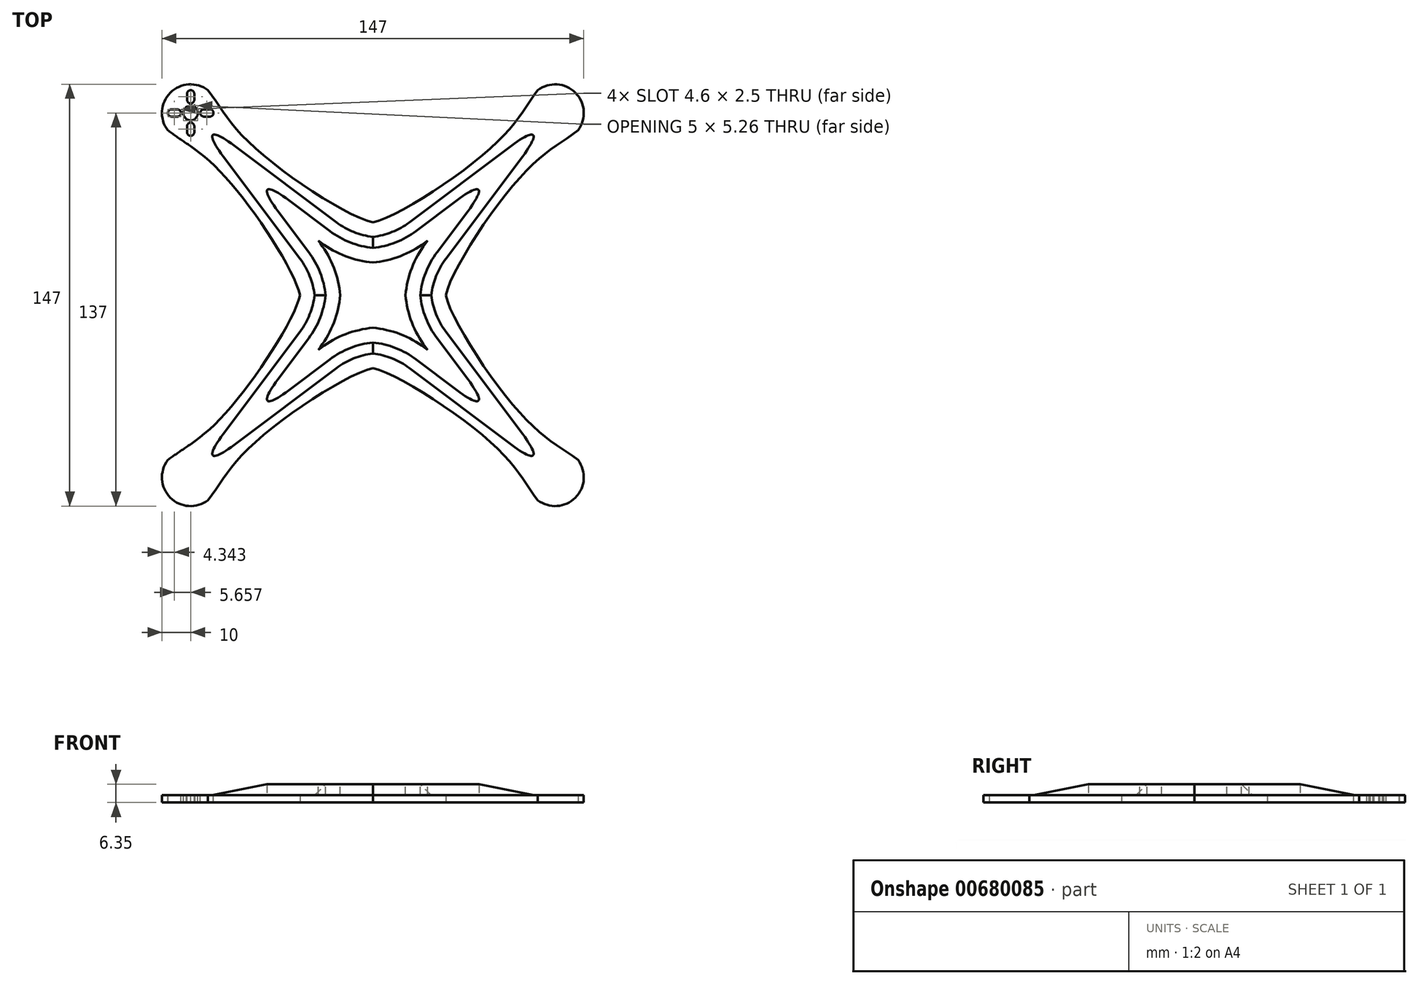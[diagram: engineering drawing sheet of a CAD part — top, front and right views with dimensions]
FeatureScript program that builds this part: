
annotation { "Feature Type Name" : "Feature", "Feature Type Description" : "" }
export const myFeature = defineFeature(function(context is Context, id is Id, definition is map)
    precondition{}
    {
        {
            var Q0;
            Q0=qCreatedBy(makeId("Top.planeOp"),FACE);
            var sketch = newSketch(context, id + "F0", { "sketchPlane" : qUnion([Q0])});
            skLineSegment(sketch, "E0", {"start": v(-50.8, 0) * mm, "end": v(50.8, 0) * mm, "construction": true});
            skLineSegment(sketch, "E1", {"start": v(0, 50.8) * mm, "end": v(0, -50.8) * mm, "construction": true});
            skLineSegment(sketch, "E2", {"start": v(0, 0) * mm, "end": v(-63.5, 63.5) * mm, "construction": true});
            skArc(sketch, "E3", {"start": v(-57.46, 71.47) * mm, "mid": v(-70.57, 70.57) * mm, "end": v(-71.47, 57.46) * mm});
            skLineSegment(sketch, "E4", {"start": v(0, 0) * mm, "end": v(0, 25.4) * mm});
            skFitSpline(sketch, "E5", {"points": [v(-57.46, 71.47) * mm, v(-42.48, 52.58) * mm, v(0, 25.4) * mm], "startDerivative": vector(33.33, -44.36) * mm, "endDerivative": vector(44.67, -9.8) * mm});
            skFitSpline(sketch, "E6.MirrorCS", {"points": [v(-71.47, 57.46) * mm, v(-52.58, 42.48) * mm, v(-25.4, 0) * mm], "startDerivative": vector(44.36, -33.33) * mm, "endDerivative": vector(9.8, -44.67) * mm});
            skFitSpline(sketch, "E7.MirrorCS", {"points": [v(-71.47, 57.46) * mm, v(-52.58, 42.48) * mm, v(-25.4, 0) * mm], "startDerivative": vector(44.36, -33.33) * mm, "endDerivative": vector(9.8, -44.67) * mm});
            skFitSpline(sketch, "E8.MirrorCS", {"points": [v(-57.46, 71.47) * mm, v(-42.48, 52.58) * mm, v(0, 25.4) * mm], "startDerivative": vector(33.33, -44.36) * mm, "endDerivative": vector(44.67, -9.8) * mm});
            skArc(sketch, "E9.MirrorCS", {"start": v(-71.47, 57.46) * mm, "mid": v(-70.57, 70.57) * mm, "end": v(-57.46, 71.47) * mm});
            skLineSegment(sketch, "E10.MirrorCS", {"start": v(0, 0) * mm, "end": v(-25.4, 0) * mm});
            skFitSpline(sketch, "E11.MirrorCS", {"points": [v(57.46, 71.47) * mm, v(42.48, 52.58) * mm, v(0, 25.4) * mm], "startDerivative": vector(-33.33, -44.36) * mm, "endDerivative": vector(-44.67, -9.8) * mm});
            skFitSpline(sketch, "E12.MirrorCS", {"points": [v(71.47, 57.46) * mm, v(52.58, 42.48) * mm, v(25.4, 0) * mm], "startDerivative": vector(-44.36, -33.33) * mm, "endDerivative": vector(-9.8, -44.67) * mm});
            skArc(sketch, "E13.MirrorCS", {"start": v(71.47, 57.46) * mm, "mid": v(70.57, 70.57) * mm, "end": v(57.46, 71.47) * mm});
            skFitSpline(sketch, "E14.MirrorCS", {"points": [v(-71.47, -57.46) * mm, v(-52.58, -42.48) * mm, v(-25.4, 0) * mm], "startDerivative": vector(44.36, 33.33) * mm, "endDerivative": vector(9.8, 44.67) * mm});
            skFitSpline(sketch, "E15.MirrorCS", {"points": [v(-57.46, -71.47) * mm, v(-42.48, -52.58) * mm, v(0, -25.4) * mm], "startDerivative": vector(33.33, 44.36) * mm, "endDerivative": vector(44.67, 9.8) * mm});
            skFitSpline(sketch, "E16.MirrorCS", {"points": [v(71.47, -57.46) * mm, v(52.58, -42.48) * mm, v(25.4, 0) * mm], "startDerivative": vector(-44.36, 33.33) * mm, "endDerivative": vector(-9.8, 44.67) * mm});
            skFitSpline(sketch, "E17.MirrorCS", {"points": [v(57.46, -71.47) * mm, v(42.48, -52.58) * mm, v(0, -25.4) * mm], "startDerivative": vector(-33.33, 44.36) * mm, "endDerivative": vector(-44.67, 9.8) * mm});
            skArc(sketch, "E18.MirrorCS", {"start": v(-71.47, -57.46) * mm, "mid": v(-70.57, -70.57) * mm, "end": v(-57.46, -71.47) * mm});
            skFitSpline(sketch, "E19.MirrorCS", {"points": [v(-71.47, -57.46) * mm, v(-52.58, -42.48) * mm, v(-25.4, 0) * mm], "startDerivative": vector(44.36, 33.33) * mm, "endDerivative": vector(9.8, 44.67) * mm});
            skArc(sketch, "E20.MirrorCS", {"start": v(-57.46, -71.47) * mm, "mid": v(-70.57, -70.57) * mm, "end": v(-71.47, -57.46) * mm});
            skArc(sketch, "E21.MirrorCS", {"start": v(71.47, -57.46) * mm, "mid": v(70.57, -70.57) * mm, "end": v(57.46, -71.47) * mm});
            skLineSegment(sketch, "E22.MirrorCS", {"start": v(0, 0) * mm, "end": v(0, -25.4) * mm});
            skLineSegment(sketch, "E23.MirrorCS", {"start": v(0, 0) * mm, "end": v(-63.5, -63.5) * mm, "construction": true});
            skLineSegment(sketch, "E24", {"start": v(-63.5, -63.5) * mm, "end": v(-63.5, 63.5) * mm});
            skSolve(sketch);
        }
        {
            var Q0;
            Q0=makeQuery(id+"F0.imprint","IMPRINT",FACE,{"disambiguationData":[TD([[makeQuery(id+"F0.imprint","IMPRINT",EDGE,{"derivedFrom":sQuery(id+"F0.wireOp",EDGE,"E4")}),-1.0]])]});
            var Q1;
            Q1=makeQuery(id+"F0.imprint","IMPRINT",FACE,{"disambiguationData":[TD([[makeQuery(id+"F0.imprint","IMPRINT",EDGE,{"derivedFrom":sQuery(id+"F0.wireOp",EDGE,"E10.MirrorCS")}),1.0]])]});
            var Q2;
            Q2=makeQuery(id+"F0.imprint","IMPRINT",FACE,{"disambiguationData":[TD([[makeQuery(id+"F0.imprint","IMPRINT",EDGE,{"derivedFrom":sQuery(id+"F0.wireOp",EDGE,"E4")}),1.0]])]});
            extrude(context, id + "F1", {"entities" : qUnion([Q0, Q1, Q2]), "depth" : 2.54 * mm, "offsetDistance" : 25.4 * mm, "symmetric" : true});
        }
        {
            var Q0;
            Q0=makeQuery(id+"F1.opExtrude","CAP_FACE",FACE,{"disambiguationData":[OSD([sQuery(id+"F0.wireOp",EDGE,"E7.MirrorCS"),sQuery(id+"F0.wireOp",EDGE,"E8.MirrorCS"),sQuery(id+"F0.wireOp",EDGE,"E9.MirrorCS"),sQuery(id+"F0.wireOp",EDGE,"E11.MirrorCS"),sQuery(id+"F0.wireOp",EDGE,"E12.MirrorCS"),sQuery(id+"F0.wireOp",EDGE,"E13.MirrorCS"),sQuery(id+"F0.wireOp",EDGE,"E16.MirrorCS"),sQuery(id+"F0.wireOp",EDGE,"E17.MirrorCS"),sQuery(id+"F0.wireOp",EDGE,"E15.MirrorCS"),sQuery(id+"F0.wireOp",EDGE,"E19.MirrorCS"),sQuery(id+"F0.wireOp",EDGE,"E20.MirrorCS"),sQuery(id+"F0.wireOp",EDGE,"E21.MirrorCS")])],"isStart":false});
            var sketch = newSketch(context, id + "F2", { "sketchPlane" : qUnion([Q0])});
            skCircle(sketch, "E25", {"center": v(-57.84, 63.5) * mm, "radius": 1.25 * mm, "construction": true});
            skCircle(sketch, "E26", {"center": v(-63.5, 57.84) * mm, "radius": 1.25 * mm, "construction": true});
            skCircle(sketch, "E27", {"center": v(-63.5, 69.16) * mm, "radius": 1.25 * mm, "construction": true});
            skCircle(sketch, "E28", {"center": v(-69.16, 63.5) * mm, "radius": 1.25 * mm, "construction": true});
            skLineSegment(sketch, "E29", {"start": v(-63.5, 69.16) * mm, "end": v(-69.16, 63.5) * mm, "construction": true});
            skLineSegment(sketch, "E30", {"start": v(-63.5, 57.84) * mm, "end": v(-69.16, 63.5) * mm, "construction": true});
            skLineSegment(sketch, "E31", {"start": v(-57.84, 63.5) * mm, "end": v(-63.5, 57.84) * mm, "construction": true});
            skLineSegment(sketch, "E32", {"start": v(-57.84, 63.5) * mm, "end": v(-63.5, 69.16) * mm, "construction": true});
            skLineSegment(sketch, "E33", {"start": v(-69.16, 63.5) * mm, "end": v(-57.84, 63.5) * mm, "construction": true});
            skArc(sketch, "E34", {"start": v(-64.75, 68.1) * mm, "mid": v(-63.5, 66.86) * mm, "end": v(-62.25, 68.1) * mm});
            skArc(sketch, "E35", {"start": v(-62.25, 70.2) * mm, "mid": v(-63.5, 71.46) * mm, "end": v(-64.75, 70.2) * mm});
            skLineSegment(sketch, "E36", {"start": v(-64.75, 68.1) * mm, "end": v(-64.75, 70.2) * mm});
            skLineSegment(sketch, "E37", {"start": v(-62.25, 70.2) * mm, "end": v(-62.25, 68.1) * mm});
            skLineSegment(sketch, "E38", {"start": v(-63.5, 68.1) * mm, "end": v(-63.5, 70.2) * mm, "construction": true});
            skArc(sketch, "E39", {"start": v(-58.9, 64.75) * mm, "mid": v(-60.14, 63.5) * mm, "end": v(-58.9, 62.25) * mm});
            skArc(sketch, "E40", {"start": v(-56.8, 62.25) * mm, "mid": v(-55.54, 63.5) * mm, "end": v(-56.8, 64.75) * mm});
            skLineSegment(sketch, "E41", {"start": v(-58.9, 64.75) * mm, "end": v(-56.8, 64.75) * mm});
            skLineSegment(sketch, "E42", {"start": v(-56.8, 62.25) * mm, "end": v(-58.9, 62.25) * mm});
            skLineSegment(sketch, "E43", {"start": v(-58.9, 63.5) * mm, "end": v(-56.8, 63.5) * mm, "construction": true});
            skArc(sketch, "E44", {"start": v(-64.75, 56.8) * mm, "mid": v(-63.5, 55.54) * mm, "end": v(-62.25, 56.8) * mm});
            skArc(sketch, "E45", {"start": v(-62.25, 58.9) * mm, "mid": v(-63.5, 60.14) * mm, "end": v(-64.75, 58.9) * mm});
            skLineSegment(sketch, "E46", {"start": v(-64.75, 56.8) * mm, "end": v(-64.75, 58.9) * mm});
            skLineSegment(sketch, "E47", {"start": v(-62.25, 58.9) * mm, "end": v(-62.25, 56.8) * mm});
            skLineSegment(sketch, "E48", {"start": v(-63.5, 56.8) * mm, "end": v(-63.5, 58.9) * mm, "construction": true});
            skArc(sketch, "E49", {"start": v(-70.2, 64.75) * mm, "mid": v(-71.46, 63.5) * mm, "end": v(-70.2, 62.25) * mm});
            skArc(sketch, "E50", {"start": v(-68.1, 62.25) * mm, "mid": v(-66.86, 63.5) * mm, "end": v(-68.1, 64.75) * mm});
            skLineSegment(sketch, "E51", {"start": v(-70.2, 64.75) * mm, "end": v(-68.1, 64.75) * mm});
            skLineSegment(sketch, "E52", {"start": v(-68.1, 62.25) * mm, "end": v(-70.2, 62.25) * mm});
            skLineSegment(sketch, "E53", {"start": v(-70.2, 63.5) * mm, "end": v(-68.1, 63.5) * mm, "construction": true});
            skLineSegment(sketch, "E54", {"start": v(-63.5, 69.16) * mm, "end": v(-63.5, 57.84) * mm, "construction": true});
            skCircle(sketch, "E55.cCircle", {"center": v(-63.5, 63.5) * mm, "radius": 2.5 * mm, "construction": true});
            skLineSegment(sketch, "E55.0", {"start": v(-61, 62.69) * mm, "end": v(-61.95, 61.37) * mm});
            skLineSegment(sketch, "E55.1", {"start": v(-61.95, 61.37) * mm, "end": v(-63.5, 60.87) * mm});
            skLineSegment(sketch, "E55.2", {"start": v(-63.5, 60.87) * mm, "end": v(-65.05, 61.37) * mm});
            skLineSegment(sketch, "E55.3", {"start": v(-65.05, 61.37) * mm, "end": v(-66, 62.69) * mm});
            skLineSegment(sketch, "E55.4", {"start": v(-66, 62.69) * mm, "end": v(-66, 64.31) * mm});
            skLineSegment(sketch, "E55.5", {"start": v(-66, 64.31) * mm, "end": v(-65.05, 65.63) * mm});
            skLineSegment(sketch, "E55.6", {"start": v(-65.05, 65.63) * mm, "end": v(-63.5, 66.13) * mm});
            skLineSegment(sketch, "E55.7", {"start": v(-63.5, 66.13) * mm, "end": v(-61.95, 65.63) * mm});
            skLineSegment(sketch, "E55.8", {"start": v(-61.95, 65.63) * mm, "end": v(-61, 64.31) * mm});
            skLineSegment(sketch, "E55.9", {"start": v(-61, 64.31) * mm, "end": v(-61, 62.69) * mm});
            skPoint(sketch, "E55.0.midPoint", {"position": v(-61.48, 62.03) * mm});
            skSolve(sketch);
        }
        {
            var Q0;
            Q0 = qSketchRegion(id + "F2", true);
            extrude(context, id + "F3", {"entities" : qUnion([Q0]), "operationType" : NewBodyOperationType.REMOVE, "endBound" : BoundingType.THROUGH_ALL, "oppositeDirection" : true, "depth" : 25.4 * mm, "offsetDistance" : 25.4 * mm});
        }
        {
            var Q0;
            Q0=makeQuery(id+"F1.opExtrude","CAP_FACE",FACE,{"disambiguationData":[OSD([sQuery(id+"F0.wireOp",EDGE,"E7.MirrorCS"),sQuery(id+"F0.wireOp",EDGE,"E8.MirrorCS"),sQuery(id+"F0.wireOp",EDGE,"E9.MirrorCS"),sQuery(id+"F0.wireOp",EDGE,"E11.MirrorCS"),sQuery(id+"F0.wireOp",EDGE,"E12.MirrorCS"),sQuery(id+"F0.wireOp",EDGE,"E13.MirrorCS"),sQuery(id+"F0.wireOp",EDGE,"E16.MirrorCS"),sQuery(id+"F0.wireOp",EDGE,"E17.MirrorCS"),sQuery(id+"F0.wireOp",EDGE,"E15.MirrorCS"),sQuery(id+"F0.wireOp",EDGE,"E19.MirrorCS"),sQuery(id+"F0.wireOp",EDGE,"E20.MirrorCS"),sQuery(id+"F0.wireOp",EDGE,"E21.MirrorCS")])],"isStart":false});
            var sketch = newSketch(context, id + "F4", { "sketchPlane" : qUnion([Q0])});
            skLineSegment(sketch, "E56", {"start": v(-63.5, -63.5) * mm, "end": v(0, 0) * mm, "construction": true});
            skLineSegment(sketch, "E57", {"start": v(0, 0) * mm, "end": v(0, -25.4) * mm, "construction": true});
            skLineSegment(sketch, "E58", {"start": v(0, -25.4) * mm, "end": v(-25.4, -25.4) * mm, "construction": true});
            skLineSegment(sketch, "E59", {"start": v(-25.4, -25.4) * mm, "end": v(-25.4, 0) * mm, "construction": true});
            skLineSegment(sketch, "E60", {"start": v(-25.4, 0) * mm, "end": v(0, 0) * mm, "construction": true});
            skLineSegment(sketch, "E61", {"start": v(-63.5, -63.5) * mm, "end": v(-25.4, -12.7) * mm});
            skLineSegment(sketch, "E62", {"start": v(-63.5, -63.5) * mm, "end": v(-12.7, -25.4) * mm});
            skArc(sketch, "E63", {"start": v(0, -20.32) * mm, "mid": v(-6.69, -22.02) * mm, "end": v(-12.7, -25.4) * mm});
            skArc(sketch, "E64.MirrorCS", {"start": v(-20.32, 0) * mm, "mid": v(-22.02, -6.69) * mm, "end": v(-25.4, -12.7) * mm});
            skArc(sketch, "E65.1.0", {"start": v(0, -20.32) * mm, "mid": v(6.69, -22.02) * mm, "end": v(12.7, -25.4) * mm});
            skLineSegment(sketch, "E65.1.1", {"start": v(63.5, -63.5) * mm, "end": v(12.7, -25.4) * mm});
            skLineSegment(sketch, "E65.1.2", {"start": v(63.5, -63.5) * mm, "end": v(25.4, -12.7) * mm});
            skArc(sketch, "E65.1.3", {"start": v(20.32, 0) * mm, "mid": v(22.02, -6.69) * mm, "end": v(25.4, -12.7) * mm});
            skArc(sketch, "E65.2.0", {"start": v(20.32, 0) * mm, "mid": v(22.02, 6.69) * mm, "end": v(25.4, 12.7) * mm});
            skLineSegment(sketch, "E65.2.1", {"start": v(63.5, 63.5) * mm, "end": v(25.4, 12.7) * mm});
            skLineSegment(sketch, "E65.2.2", {"start": v(63.5, 63.5) * mm, "end": v(12.7, 25.4) * mm});
            skArc(sketch, "E65.2.3", {"start": v(0, 20.32) * mm, "mid": v(6.69, 22.02) * mm, "end": v(12.7, 25.4) * mm});
            skArc(sketch, "E65.3.0", {"start": v(0, 20.32) * mm, "mid": v(-6.69, 22.02) * mm, "end": v(-12.7, 25.4) * mm});
            skLineSegment(sketch, "E65.3.1", {"start": v(-63.5, 63.5) * mm, "end": v(-12.7, 25.4) * mm});
            skLineSegment(sketch, "E65.3.2", {"start": v(-63.5, 63.5) * mm, "end": v(-25.4, 12.7) * mm});
            skArc(sketch, "E65.3.3", {"start": v(-20.32, 0) * mm, "mid": v(-22.02, 6.69) * mm, "end": v(-25.4, 12.7) * mm});
            skPoint(sketch, "E65.center", {"position": v(0, 0) * mm});
            skSolve(sketch);
        }
        {
            var Q0;
            Q0=makeQuery(id+"F4.imprint","IMPRINT",FACE,{"disambiguationData":[TD([[makeQuery(id+"F4.imprint","IMPRINT",EDGE,{"derivedFrom":sQuery(id+"F4.wireOp",EDGE,"E61")}),-1.0]])]});
            var Q1;
            {var subQ18=sQuery(id+"F4.wireOp",EDGE,"E63");Q1=makeQuery(id+"F4.imprint","IMPRINT",FACE,{"disambiguationData":[TD([[makeQuery(id+"F4.imprint","IMPRINT",EDGE,{"derivedFrom":subQ18}),-1.0]])]});}
            extrude(context, id + "F5", {"entities" : qUnion([Q0, Q1]), "operationType" : NewBodyOperationType.ADD, "depth" : 3.8 * mm, "offsetDistance" : 25.4 * mm});
        }
        {
            var Q0;
            Q0=makeQuery(id+"F5.opExtrude","CAP_FACE",FACE,{"disambiguationData":[OSD([sQuery(id+"F2.wireOp",EDGE,"E55.0"),sQuery(id+"F4.wireOp",EDGE,"E61"),sQuery(id+"F4.wireOp",EDGE,"E62"),sQuery(id+"F4.wireOp",EDGE,"E63"),sQuery(id+"F4.wireOp",EDGE,"E64.MirrorCS"),sQuery(id+"F4.wireOp",EDGE,"E65.1.0"),sQuery(id+"F4.wireOp",EDGE,"E65.1.1"),sQuery(id+"F4.wireOp",EDGE,"E65.1.2"),sQuery(id+"F4.wireOp",EDGE,"E65.1.3"),sQuery(id+"F4.wireOp",EDGE,"E65.2.0"),sQuery(id+"F4.wireOp",EDGE,"E65.2.1"),sQuery(id+"F4.wireOp",EDGE,"E65.2.2"),sQuery(id+"F4.wireOp",EDGE,"E65.2.3"),sQuery(id+"F4.wireOp",EDGE,"E65.3.0"),sQuery(id+"F4.wireOp",EDGE,"E65.3.1"),sQuery(id+"F4.wireOp",EDGE,"E65.3.2"),sQuery(id+"F4.wireOp",EDGE,"E65.3.3")])],"isStart":false});
            chamfer(context, id + "F6", {"entities" : qUnion([Q0]), "width" : 3.8 * mm, "tangentPropagation" : true});
        }
        {
            var Q0;
            Q0=makeQuery(id+"F6.opChamfer","BLEND_EDGE",EDGE,{"blendedFrom":[makeQuery(id+"F5.opExtrude","CAP_EDGE",EDGE,{"disambiguationData":[OSD([sQuery(id+"F4.wireOp",EDGE,"E61")])],"isStart":false}),makeQuery(id+"F5.opExtrude","CAP_EDGE",EDGE,{"disambiguationData":[OSD([sQuery(id+"F4.wireOp",EDGE,"E62")])],"isStart":false})],"blendedInto":[]});
            var Q1;
            Q1=makeQuery(id+"F6.opChamfer","BLEND_EDGE",EDGE,{"blendedFrom":[makeQuery(id+"F5.opExtrude","CAP_EDGE",EDGE,{"disambiguationData":[OSD([sQuery(id+"F4.wireOp",EDGE,"E65.3.1")])],"isStart":false}),makeQuery(id+"F5.opExtrude","CAP_EDGE",EDGE,{"disambiguationData":[OSD([sQuery(id+"F4.wireOp",EDGE,"E65.3.2")])],"isStart":false})],"blendedInto":[]});
            var Q2;
            Q2=makeQuery(id+"F6.opChamfer","BLEND_EDGE",EDGE,{"blendedFrom":[makeQuery(id+"F5.opExtrude","CAP_EDGE",EDGE,{"disambiguationData":[OSD([sQuery(id+"F4.wireOp",EDGE,"E65.1.1")])],"isStart":false}),makeQuery(id+"F5.opExtrude","CAP_EDGE",EDGE,{"disambiguationData":[OSD([sQuery(id+"F4.wireOp",EDGE,"E65.1.2")])],"isStart":false})],"blendedInto":[]});
            var Q3;
            Q3=makeQuery(id+"F6.opChamfer","BLEND_EDGE",EDGE,{"blendedFrom":[makeQuery(id+"F5.opExtrude","CAP_EDGE",EDGE,{"disambiguationData":[OSD([sQuery(id+"F4.wireOp",EDGE,"E65.2.1")])],"isStart":false}),makeQuery(id+"F5.opExtrude","CAP_EDGE",EDGE,{"disambiguationData":[OSD([sQuery(id+"F4.wireOp",EDGE,"E65.2.2")])],"isStart":false})],"blendedInto":[]});
            fillet(context, id + "F7", {"entities" : qUnion([Q0, Q1, Q2, Q3]), "radius" : 3.8 * mm, "tangentPropagation" : true, "defaultsChanged" : false, "vertexSettings" : [], "allowEdgeOverflow" : false});
        }
        {
            var Q0;
            Q0=makeQuery(id+"F5.opExtrude","CAP_FACE",FACE,{"disambiguationData":[OSD([sQuery(id+"F2.wireOp",EDGE,"E55.0"),sQuery(id+"F4.wireOp",EDGE,"E61"),sQuery(id+"F4.wireOp",EDGE,"E62"),sQuery(id+"F4.wireOp",EDGE,"E63"),sQuery(id+"F4.wireOp",EDGE,"E64.MirrorCS"),sQuery(id+"F4.wireOp",EDGE,"E65.1.0"),sQuery(id+"F4.wireOp",EDGE,"E65.1.1"),sQuery(id+"F4.wireOp",EDGE,"E65.1.2"),sQuery(id+"F4.wireOp",EDGE,"E65.1.3"),sQuery(id+"F4.wireOp",EDGE,"E65.2.0"),sQuery(id+"F4.wireOp",EDGE,"E65.2.1"),sQuery(id+"F4.wireOp",EDGE,"E65.2.2"),sQuery(id+"F4.wireOp",EDGE,"E65.2.3"),sQuery(id+"F4.wireOp",EDGE,"E65.3.0"),sQuery(id+"F4.wireOp",EDGE,"E65.3.1"),sQuery(id+"F4.wireOp",EDGE,"E65.3.2"),sQuery(id+"F4.wireOp",EDGE,"E65.3.3")])],"isStart":false});
            var sketch = newSketch(context, id + "F8", { "sketchPlane" : qUnion([Q0])});
            skLineSegment(sketch, "E66.0.0", {"start": v(14.99, -22.35) * mm, "end": v(29.36, -33.13) * mm});
            skEllipticalArc(sketch, "E66.0.1", {});
            skLineSegment(sketch, "E66.0.2", {"start": v(33.13, -29.36) * mm, "end": v(22.35, -14.99) * mm});
            skArc(sketch, "E66.0.3", {"start": v(22.35, -14.99) * mm, "mid": v(18.4, -7.9) * mm, "end": v(16.49, 0) * mm});
            skArc(sketch, "E66.0.4", {"start": v(16.49, 0) * mm, "mid": v(18.4, 7.9) * mm, "end": v(22.35, 14.99) * mm});
            skLineSegment(sketch, "E66.0.5", {"start": v(22.35, 14.99) * mm, "end": v(33.13, 29.36) * mm});
            skEllipticalArc(sketch, "E66.0.6", {});
            skLineSegment(sketch, "E66.0.7", {"start": v(29.36, 33.13) * mm, "end": v(14.99, 22.35) * mm});
            skArc(sketch, "E66.0.8", {"start": v(14.99, 22.35) * mm, "mid": v(7.9, 18.4) * mm, "end": v(0, 16.49) * mm});
            skArc(sketch, "E66.0.9", {"start": v(0, 16.49) * mm, "mid": v(-7.9, 18.4) * mm, "end": v(-14.99, 22.35) * mm});
            skLineSegment(sketch, "E66.0.10", {"start": v(-14.99, 22.35) * mm, "end": v(-29.36, 33.13) * mm});
            skEllipticalArc(sketch, "E66.0.11", {});
            skLineSegment(sketch, "E66.0.12", {"start": v(-33.13, 29.36) * mm, "end": v(-22.35, 14.99) * mm});
            skArc(sketch, "E66.0.13", {"start": v(-22.35, 14.99) * mm, "mid": v(-18.4, 7.9) * mm, "end": v(-16.49, 0) * mm});
            skArc(sketch, "E66.0.14", {"start": v(-16.49, 0) * mm, "mid": v(-18.4, -7.9) * mm, "end": v(-22.35, -14.99) * mm});
            skLineSegment(sketch, "E66.0.15", {"start": v(-22.35, -14.99) * mm, "end": v(-33.13, -29.36) * mm});
            skEllipticalArc(sketch, "E66.0.16", {});
            skLineSegment(sketch, "E66.0.17", {"start": v(-29.36, -33.13) * mm, "end": v(-14.99, -22.35) * mm});
            skArc(sketch, "E66.0.18", {"start": v(-14.99, -22.35) * mm, "mid": v(-7.9, -18.4) * mm, "end": v(0, -16.49) * mm});
            skArc(sketch, "E66.0.19", {"start": v(0, -16.49) * mm, "mid": v(7.9, -18.4) * mm, "end": v(14.99, -22.35) * mm});
            skArc(sketch, "E67.0", {"start": v(0, -11.38) * mm, "mid": v(9.5, -13.58) * mm, "end": v(18.03, -18.29) * mm});
            skArc(sketch, "E67.1", {"start": v(-18.03, -18.29) * mm, "mid": v(-9.5, -13.58) * mm, "end": v(0, -11.38) * mm});
            skLineSegment(sketch, "E67.2", {"start": v(-19.05, -19.05) * mm, "end": v(-18.03, -18.29) * mm});
            skLineSegment(sketch, "E67.3", {"start": v(-18.29, -18.03) * mm, "end": v(-19.05, -19.05) * mm});
            skArc(sketch, "E67.4", {"start": v(-11.38, 0) * mm, "mid": v(-13.58, -9.5) * mm, "end": v(-18.29, -18.03) * mm});
            skLineSegment(sketch, "E67.5", {"start": v(18.29, 18.03) * mm, "end": v(19.05, 19.05) * mm});
            skArc(sketch, "E67.6", {"start": v(11.38, 0) * mm, "mid": v(13.58, 9.5) * mm, "end": v(18.29, 18.03) * mm});
            skArc(sketch, "E67.7", {"start": v(18.29, -18.03) * mm, "mid": v(13.58, -9.5) * mm, "end": v(11.38, 0) * mm});
            skLineSegment(sketch, "E67.8", {"start": v(19.05, -19.05) * mm, "end": v(18.29, -18.03) * mm});
            skLineSegment(sketch, "E67.9", {"start": v(19.05, 19.05) * mm, "end": v(18.03, 18.29) * mm});
            skArc(sketch, "E67.10", {"start": v(18.03, 18.29) * mm, "mid": v(9.5, 13.58) * mm, "end": v(0, 11.38) * mm});
            skArc(sketch, "E67.11", {"start": v(0, 11.38) * mm, "mid": v(-9.5, 13.58) * mm, "end": v(-18.03, 18.29) * mm});
            skLineSegment(sketch, "E67.12", {"start": v(-18.03, 18.29) * mm, "end": v(-19.05, 19.05) * mm});
            skLineSegment(sketch, "E67.13", {"start": v(-19.05, 19.05) * mm, "end": v(-18.29, 18.03) * mm});
            skLineSegment(sketch, "E67.14", {"start": v(18.03, -18.29) * mm, "end": v(19.05, -19.05) * mm});
            skArc(sketch, "E67.15", {"start": v(-18.29, 18.03) * mm, "mid": v(-13.58, 9.5) * mm, "end": v(-11.38, 0) * mm});
            const initialGuessF8  = {"E66.0.1": [0.017509231636792525, -0.01750923163679253, 0.7071067811865472, -0.7071067811865478, 0.027208842312748255, 0.00381, 5.507787810568834, 0.7753974966107542], "E66.0.6": [0.017509231636792535, 0.017509231636792525, -0.7071067811865479, -0.7071067811865472, 0.027208842312748244, 0.00381, 2.366195156979039, 3.916990150200544], "E66.0.11": [-0.01750923163679253, 0.017509231636792535, 0.7071067811865472, -0.7071067811865479, 0.02720884231274825, 0.00381, 2.366195156979041, 3.916990150200545], "E66.0.16": [-0.01750923163679253, -0.01750923163679251, -0.7071067811865477, -0.7071067811865474, 0.02720884231274829, 0.00381, 5.507787810568834, 0.7753974966107542]};
            skSetInitialGuess(sketch, initialGuessF8);
            skSolve(sketch);
        }
        {
            var Q0;
            Q0=makeQuery(id+"F8.imprint","IMPRINT",FACE,{"disambiguationData":[TD([[makeQuery(id+"F8.imprint","IMPRINT",EDGE,{"derivedFrom":sQuery(id+"F8.wireOp",EDGE,"E67.0")}),1.0]])]});
            var Q1;
            Q1 = qConstructionFilter(qBodyType(qCreatedBy(id + "F8" ,EDGE), BodyType.WIRE), ConstructionObject.NO);
            var Q2;
            Q2=makeQuery(id+"F1.opExtrude","CAP_FACE",FACE,{"disambiguationData":[OSD([sQuery(id+"F0.wireOp",EDGE,"E7.MirrorCS"),sQuery(id+"F0.wireOp",EDGE,"E8.MirrorCS"),sQuery(id+"F0.wireOp",EDGE,"E9.MirrorCS"),sQuery(id+"F0.wireOp",EDGE,"E11.MirrorCS"),sQuery(id+"F0.wireOp",EDGE,"E12.MirrorCS"),sQuery(id+"F0.wireOp",EDGE,"E13.MirrorCS"),sQuery(id+"F0.wireOp",EDGE,"E16.MirrorCS"),sQuery(id+"F0.wireOp",EDGE,"E17.MirrorCS"),sQuery(id+"F0.wireOp",EDGE,"E15.MirrorCS"),sQuery(id+"F0.wireOp",EDGE,"E19.MirrorCS"),sQuery(id+"F0.wireOp",EDGE,"E20.MirrorCS"),sQuery(id+"F0.wireOp",EDGE,"E21.MirrorCS")])],"isStart":false});
            extrude(context, id + "F9", {"entities" : qUnion([Q0]), "operationType" : NewBodyOperationType.REMOVE, "surfaceEntities" : qUnion([Q1]), "endBound" : BoundingType.UP_TO_SURFACE, "oppositeDirection" : true, "depth" : 25.4 * mm, "endBoundEntityFace" : qUnion([Q2]), "offsetDistance" : 25.4 * mm});
        }
    });
